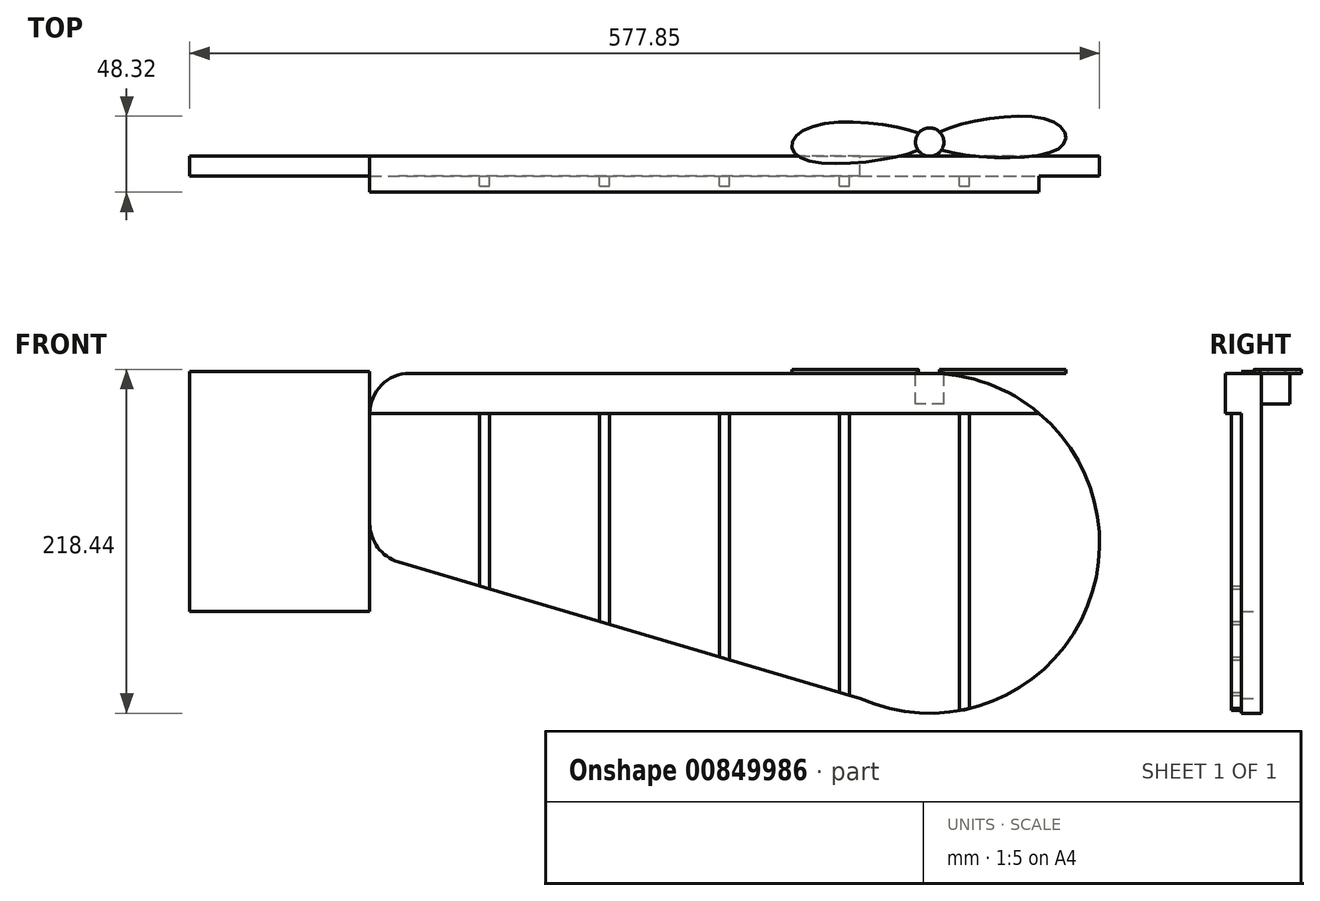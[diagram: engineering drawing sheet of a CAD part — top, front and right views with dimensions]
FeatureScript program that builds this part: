
annotation { "Feature Type Name" : "Feature", "Feature Type Description" : "" }
export const myFeature = defineFeature(function(context is Context, id is Id, definition is map)
    precondition{}
    {
        {
            var Q0;
            Q0=qCreatedBy(makeId("Front.planeOp"),FACE);
            var sketch = newSketch(context, id + "F0", { "sketchPlane" : qUnion([Q0])});
            skLineSegment(sketch, "E0", {"start": v(0, 18.97) * mm, "end": v(0, 88.9) * mm});
            skLineSegment(sketch, "E1", {"start": v(25.4, 114.3) * mm, "end": v(355.6, 114.3) * mm});
            skLineSegment(sketch, "E2", {"start": v(311.37, -92.12) * mm, "end": v(18.2, -5.38) * mm});
            skArc(sketch, "E3", {"start": v(311.37, -92.12) * mm, "mid": v(461.15, -16.27) * mm, "end": v(355.6, 114.3) * mm});
            skPoint(sketch, "E4.visualSharp", {"position": v(0, 114.3) * mm});
            skArc(sketch, "E4.filletArc", {"start": v(25.4, 114.3) * mm, "mid": v(7.44, 106.86) * mm, "end": v(0, 88.9) * mm});
            skPoint(sketch, "E5.visualSharp", {"position": v(0, 0) * mm});
            skArc(sketch, "E5.filletArc", {"start": v(0, 18.97) * mm, "mid": v(5.05, 3.77) * mm, "end": v(18.2, -5.38) * mm});
            skSolve(sketch);
        }
        {
            var Q0;
            Q0=makeQuery(id+"F0.imprint","IMPRINT",FACE,{"disambiguationData":[TD([[makeQuery(id+"F0.imprint","IMPRINT",EDGE,{"derivedFrom":sQuery(id+"F0.wireOp",EDGE,"E0")}),-1.0]])]});
            extrude(context, id + "F1", {"entities" : qUnion([Q0]), "depth" : 12.7 * mm, "offsetDistance" : 25.4 * mm});
        }
        {
            var Q0;
            Q0=makeQuery(id+"F1.opExtrude","CAP_FACE",FACE,{"disambiguationData":[OSD([sQuery(id+"F0.wireOp",EDGE,"E0"),sQuery(id+"F0.wireOp",EDGE,"E1"),sQuery(id+"F0.wireOp",EDGE,"E2"),sQuery(id+"F0.wireOp",EDGE,"E3"),sQuery(id+"F0.wireOp",EDGE,"E4.filletArc"),sQuery(id+"F0.wireOp",EDGE,"E5.filletArc")])],"isStart":false});
            var sketch = newSketch(context, id + "F2", { "sketchPlane" : qUnion([Q0])});
            skLineSegment(sketch, "E6", {"start": v(0, 88.9) * mm, "end": v(425.16, 88.9) * mm});
            skSolve(sketch);
        }
        {
            var Q0;
            {var subQ0=sQuery(id+"F2.wireOp",EDGE,"E6");Q0=makeQuery(id+"F2.imprint","IMPRINT",FACE,{"disambiguationData":[TD([[makeQuery(id+"F2.imprint","IMPRINT",EDGE,{"derivedFrom":subQ0}),1.0]])]});}
            extrude(context, id + "F3", {"entities" : qUnion([Q0]), "operationType" : NewBodyOperationType.ADD, "depth" : 10.16 * mm, "offsetDistance" : 25.4 * mm});
        }
        {
            var Q0;
            Q0=makeQuery(id+"F1.opExtrude","CAP_FACE",FACE,{"disambiguationData":[OSD([sQuery(id+"F0.wireOp",EDGE,"E0"),sQuery(id+"F0.wireOp",EDGE,"E1"),sQuery(id+"F0.wireOp",EDGE,"E2"),sQuery(id+"F0.wireOp",EDGE,"E3"),sQuery(id+"F0.wireOp",EDGE,"E4.filletArc"),sQuery(id+"F0.wireOp",EDGE,"E5.filletArc")])],"isStart":false});
            var sketch = newSketch(context, id + "F4", { "sketchPlane" : qUnion([Q0])});
            skPoint(sketch, "E7", {"position": v(0, 88.9) * mm});
            skPoint(sketch, "E8", {"position": v(69.85, 88.9) * mm});
            skPoint(sketch, "E9", {"position": v(76.2, 88.9) * mm});
            skPoint(sketch, "E10", {"position": v(146.05, 88.9) * mm});
            skPoint(sketch, "E11", {"position": v(152.4, 88.9) * mm});
            skPoint(sketch, "E12", {"position": v(222.25, 88.9) * mm});
            skPoint(sketch, "E13", {"position": v(228.6, 88.9) * mm});
            skPoint(sketch, "E14", {"position": v(298.45, 88.9) * mm});
            skPoint(sketch, "E15", {"position": v(304.8, 88.9) * mm});
            skPoint(sketch, "E16", {"position": v(374.65, 88.9) * mm});
            skPoint(sketch, "E17", {"position": v(381, 88.9) * mm});
            skLineSegment(sketch, "E18", {"start": v(69.85, 88.9) * mm, "end": v(76.2, 88.9) * mm});
            skLineSegment(sketch, "E19", {"start": v(69.85, 88.9) * mm, "end": v(69.85, -20.67) * mm});
            skLineSegment(sketch, "E20", {"start": v(76.2, 88.9) * mm, "end": v(76.2, -22.54) * mm});
            skLineSegment(sketch, "E21", {"start": v(76.2, -22.54) * mm, "end": v(69.85, -20.67) * mm});
            skLineSegment(sketch, "E22", {"start": v(146.05, 88.9) * mm, "end": v(146.05, -43.21) * mm});
            skLineSegment(sketch, "E23", {"start": v(152.4, 88.9) * mm, "end": v(152.4, -45.09) * mm});
            skLineSegment(sketch, "E24", {"start": v(152.4, -45.09) * mm, "end": v(146.05, -43.21) * mm});
            skLineSegment(sketch, "E25", {"start": v(222.25, 88.9) * mm, "end": v(222.25, -65.76) * mm});
            skLineSegment(sketch, "E26", {"start": v(228.6, 88.9) * mm, "end": v(228.6, -67.63) * mm});
            skLineSegment(sketch, "E27", {"start": v(228.6, -67.63) * mm, "end": v(222.25, -65.76) * mm});
            skLineSegment(sketch, "E28", {"start": v(298.45, 88.9) * mm, "end": v(298.45, -88.3) * mm});
            skLineSegment(sketch, "E29", {"start": v(304.8, 88.9) * mm, "end": v(304.8, -90.18) * mm});
            skLineSegment(sketch, "E30", {"start": v(304.8, -90.18) * mm, "end": v(298.45, -88.3) * mm});
            skLineSegment(sketch, "E31", {"start": v(381, 88.9) * mm, "end": v(381, -98.57) * mm});
            skLineSegment(sketch, "E32", {"start": v(374.65, 88.9) * mm, "end": v(374.65, -99.9) * mm});
            skLineSegment(sketch, "E33", {"start": v(374.65, -99.9) * mm, "end": v(381, -98.57) * mm});
            skSolve(sketch);
        }
        {
            var Q0;
            Q0=makeQuery(id+"F1.opExtrude","SWEPT_BODY",BODY,{"disambiguationData":[OSD([sQuery(id+"F0.wireOp",EDGE,"E0"),sQuery(id+"F0.wireOp",EDGE,"E1"),sQuery(id+"F0.wireOp",EDGE,"E2"),sQuery(id+"F0.wireOp",EDGE,"E3"),sQuery(id+"F0.wireOp",EDGE,"E4.filletArc"),sQuery(id+"F0.wireOp",EDGE,"E5.filletArc")])]});
            transform(context, id + "F5", {"entities" : qUnion([Q0]), "transformType" : TransformType.TRANSLATION_3D, "dx" : 0 * mm, "dy" : 0 * mm, "dz" : 0 * mm, "makeCopy" : true});
        }
        {
            var Q0;
            Q0=qCreatedBy(makeId("Front.planeOp"),FACE);
            var sketch = newSketch(context, id + "F6", { "sketchPlane" : qUnion([Q0])});
            skLineSegment(sketch, "E34.bottom", {"start": v(0, -36.94) * mm, "end": v(-114.3, -36.94) * mm});
            skLineSegment(sketch, "E34.top", {"start": v(0, 115.46) * mm, "end": v(-114.3, 115.46) * mm});
            skLineSegment(sketch, "E34.left", {"start": v(0, -36.94) * mm, "end": v(0, 115.46) * mm});
            skLineSegment(sketch, "E34.right", {"start": v(-114.3, -36.94) * mm, "end": v(-114.3, 115.46) * mm});
            skSolve(sketch);
        }
        {
            var Q0;
            Q0=makeQuery(id+"F6.imprint","IMPRINT",FACE,{"disambiguationData":[TD([[makeQuery(id+"F6.imprint","IMPRINT",EDGE,{"derivedFrom":sQuery(id+"F6.wireOp",EDGE,"E34.bottom")}),-1.0]])]});
            extrude(context, id + "F7", {"entities" : qUnion([Q0]), "depth" : 12.7 * mm, "offsetDistance" : 25.4 * mm});
        }
        {
            var Q0;
            {var subQ0=sQuery(id+"F0.wireOp",EDGE,"E1");Q0=makeQuery(id+"F3.boolean.opBoolean","MERGE",FACE,{"derivedFrom":[makeQuery(id+"F1.opExtrude","SWEPT_FACE",FACE,{"disambiguationData":[OSD([subQ0])]}),makeQuery(id+"F3.opExtrude","SWEPT_FACE",FACE,{"disambiguationData":[OSD([subQ0])]})]});}
            var sketch = newSketch(context, id + "F8", { "sketchPlane" : qUnion([Q0])});
            skCircle(sketch, "E35", {"center": v(355.63, 9.02) * mm, "radius": 9.02 * mm});
            skPoint(sketch, "E35.first.point", {"position": v(355.6, 0) * mm});
            skPoint(sketch, "E35.second.point", {"position": v(355.6, 18.03) * mm});
            skPoint(sketch, "E35.third.point", {"position": v(346.75, 7.48) * mm});
            skSolve(sketch);
        }
        {
            var Q0;
            Q0=makeQuery(id+"F8.imprint","IMPRINT",FACE,{"disambiguationData":[TD([[makeQuery(id+"F8.imprint","IMPRINT",EDGE,{"derivedFrom":sQuery(id+"F8.wireOp",EDGE,"E35")}),1.0]])]});
            extrude(context, id + "F9", {"entities" : qUnion([Q0]), "oppositeDirection" : true, "depth" : 19.56 * mm, "offsetDistance" : 25.4 * mm});
        }
        {
            var Q0;
            Q0=makeQuery(id+"F9.opExtrude","CAP_FACE",FACE,{"disambiguationData":[OSD([sQuery(id+"F8.wireOp",EDGE,"E35")])],"isStart":true});
            var sketch = newSketch(context, id + "F10", { "sketchPlane" : qUnion([Q0])});
            skFitSpline(sketch, "E36", {"points": [v(355.63, 9.02) * mm, v(431.34, 23.04) * mm, v(437.62, 4.97) * mm, v(355.63, 9.02) * mm]});
            skLineSegment(sketch, "E37", {"start": v(354.34, 30.9) * mm, "end": v(355.63, -7.2) * mm, "construction": true});
            skFitSpline(sketch, "E38.MirrorC", {"points": [v(354.53, 8.98) * mm, v(278.06, 17.83) * mm, v(273.01, -0.62) * mm, v(354.53, 8.98) * mm]});
            skSolve(sketch);
        }
        {
            var Q0;
            {var subQ0=sQuery(id+"F10.wireOp",EDGE,"E38.MirrorC");var subQ1=makeQuery(id+"F9.opExtrude","CAP_EDGE",EDGE,{"disambiguationData":[OSD([sQuery(id+"F8.wireOp",EDGE,"E35")])],"isStart":true});var subQ2=makeQuery(id+"F10.imprint","INTERSECT",VERTEX,{"disambiguationData":[OD(0.0)],"derivedFrom":[subQ1,subQ0]});Q0=makeQuery(id+"F10.imprint","IMPRINT",FACE,{"disambiguationData":[TD([[makeQuery(id+"F10.imprint","IMPRINT",EDGE,{"disambiguationData":[TD([[subQ2,1.0]])],"derivedFrom":subQ0}),1.0]])]});}
            var Q1;
            {var subQ0=sQuery(id+"F10.wireOp",EDGE,"E36");var subQ1=makeQuery(id+"F9.opExtrude","CAP_EDGE",EDGE,{"disambiguationData":[OSD([sQuery(id+"F8.wireOp",EDGE,"E35")])],"isStart":true});var subQ2=makeQuery(id+"F10.imprint","INTERSECT",VERTEX,{"disambiguationData":[OD(0.0)],"derivedFrom":[subQ1,subQ0]});Q1=makeQuery(id+"F10.imprint","IMPRINT",FACE,{"disambiguationData":[TD([[makeQuery(id+"F10.imprint","IMPRINT",EDGE,{"disambiguationData":[TD([[subQ2,1.0]])],"derivedFrom":subQ0}),-1.0]])]});}
            extrude(context, id + "F11", {"entities" : qUnion([Q0, Q1]), "depth" : 2.54 * mm, "offsetDistance" : 25.4 * mm});
        }
        {
            var Q0;
            Q0=makeQuery(id+"F4.imprint","IMPRINT",FACE,{"disambiguationData":[TD([[makeQuery(id+"F4.imprint","IMPRINT",EDGE,{"derivedFrom":sQuery(id+"F4.wireOp",EDGE,"E18")}),-1.0]])]});
            var Q1;
            {var subQ0=sQuery(id+"F4.wireOp",EDGE,"E22");Q1=makeQuery(id+"F4.imprint","IMPRINT",FACE,{"disambiguationData":[TD([[makeQuery(id+"F4.imprint","IMPRINT",EDGE,{"derivedFrom":subQ0}),1.0]])]});}
            var Q2;
            {var subQ0=sQuery(id+"F4.wireOp",EDGE,"E25");Q2=makeQuery(id+"F4.imprint","IMPRINT",FACE,{"disambiguationData":[TD([[makeQuery(id+"F4.imprint","IMPRINT",EDGE,{"derivedFrom":subQ0}),1.0]])]});}
            var Q3;
            {var subQ0=sQuery(id+"F4.wireOp",EDGE,"E28");Q3=makeQuery(id+"F4.imprint","IMPRINT",FACE,{"disambiguationData":[TD([[makeQuery(id+"F4.imprint","IMPRINT",EDGE,{"derivedFrom":subQ0}),1.0]])]});}
            var Q4;
            {var subQ0=sQuery(id+"F4.wireOp",EDGE,"E31");Q4=makeQuery(id+"F4.imprint","IMPRINT",FACE,{"disambiguationData":[TD([[makeQuery(id+"F4.imprint","IMPRINT",EDGE,{"derivedFrom":subQ0}),-1.0]])]});}
            extrude(context, id + "F12", {"entities" : qUnion([Q0, Q1, Q2, Q3, Q4]), "depth" : 6.35 * mm, "offsetDistance" : 25.4 * mm});
        }
    });
